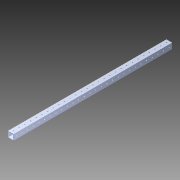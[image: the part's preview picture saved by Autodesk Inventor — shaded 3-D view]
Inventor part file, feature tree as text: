
AUTODESK INVENTOR PART (.ipt)
format: ipt  version: 2014 SP1 (Build 180222100, 222)  size: 1,561,600 bytes
history: native  units: in
note: dims shown in document units (in); Inventor stores cm internally (conversion verified against a paired STEP export)
features: extrude x2, sketch x2, pattern_circular x1, other x1, mirror x1, imported_body x1
ambient origin geometry x8: Origin, YZ Plane, XZ Plane, XY Plane, X Axis, Y Axis, Z Axis, Center Point
bodies: Body1 (feature_tree)
feature tree (8):
  pattern_circular  "CirPattern2"
  other  "1x1 tube1"
  extrude  "Extrusion1"  Depth=14.0in TaperAngle=0.0deg
  mirror  "Mirror1"
  extrude  "Extrusion2"  [1 undecoded]
  imported_body  "Base1"
  sketch  "Sketch1"  dims[d0=38.0in d1=0.0in d2=14.0in d3=0.0in]
  sketch  "Sketch3"
note: 1 required parameter value undecoded (feature->parameter linkage not recoverable at this tier; creation-order binding heuristic only, values carry confidence <= 0.55)
